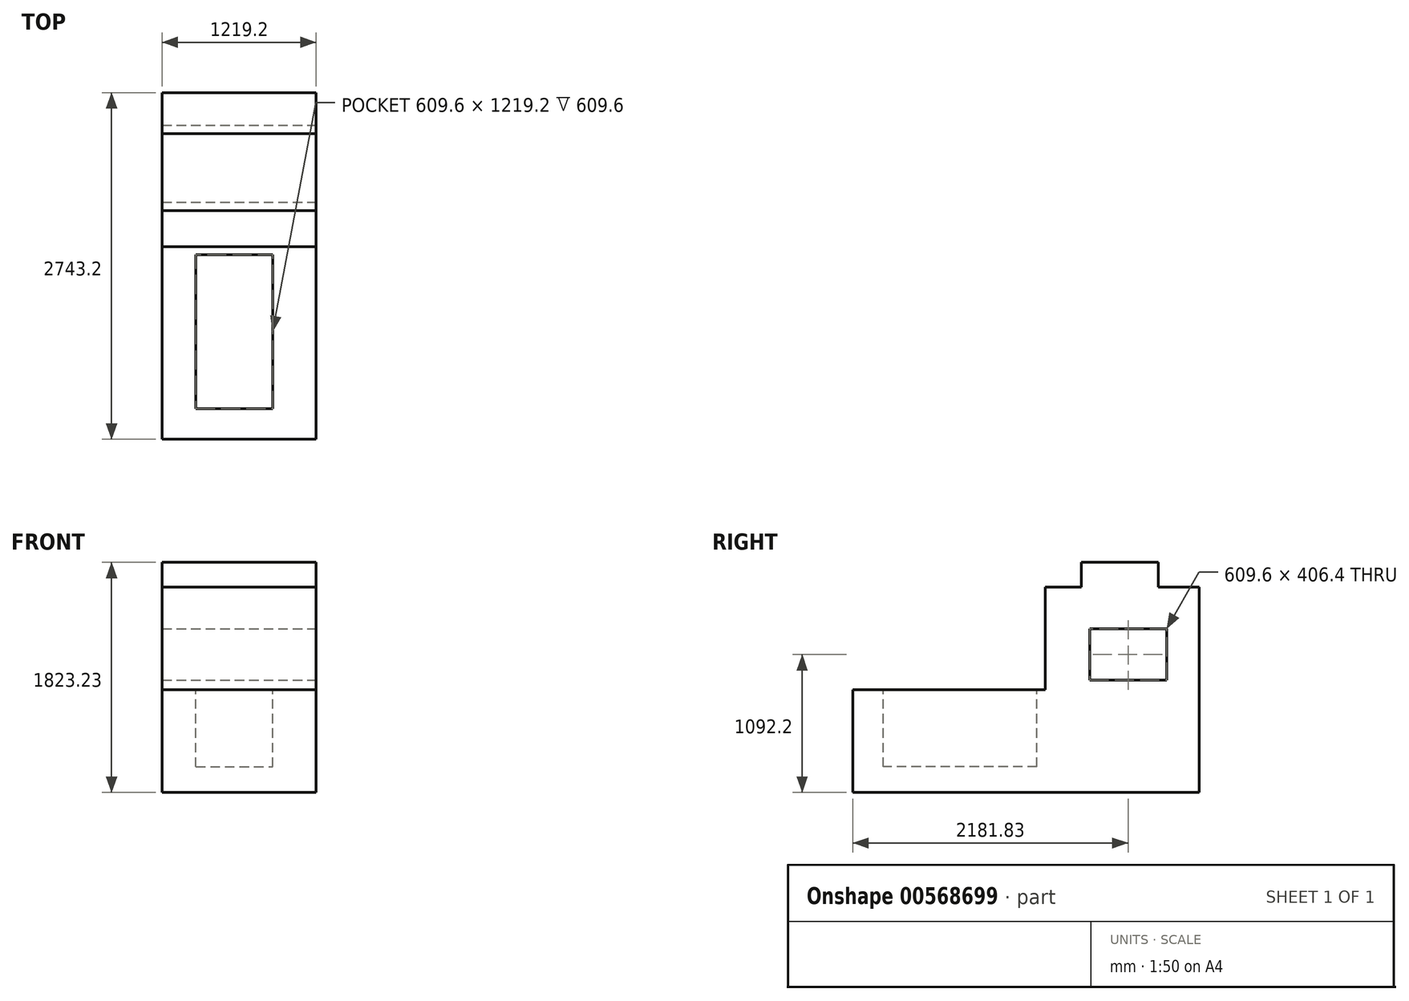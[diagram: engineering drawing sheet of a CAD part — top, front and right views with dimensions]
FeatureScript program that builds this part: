
annotation { "Feature Type Name" : "Feature", "Feature Type Description" : "" }
export const myFeature = defineFeature(function(context is Context, id is Id, definition is map)
    precondition{}
    {
        {
            var Q0;
            Q0=qCreatedBy(makeId("Front.planeOp"),FACE);
            var sketch = newSketch(context, id + "F0", { "sketchPlane" : qUnion([Q0])});
            skLineSegment(sketch, "E0.bottom", {"start": v(0, 0) * mm, "end": v(1219.2, 0) * mm});
            skLineSegment(sketch, "E0.top", {"start": v(0, 812.8) * mm, "end": v(1219.2, 812.8) * mm});
            skLineSegment(sketch, "E0.left", {"start": v(0, 0) * mm, "end": v(0, 812.8) * mm});
            skLineSegment(sketch, "E0.right", {"start": v(1219.2, 0) * mm, "end": v(1219.2, 812.8) * mm});
            skSolve(sketch);
        }
        {
            var Q0;
            Q0 = qSketchRegion(id + "F0", true);
            extrude(context, id + "F1", {"entities" : qUnion([Q0]), "depth" : 2743.2 * mm, "offsetDistance" : 25.4 * mm});
        }
        {
            var Q0;
            Q0=makeQuery(id+"F1.opExtrude","SWEPT_FACE",FACE,{"disambiguationData":[OSD([sQuery(id+"F0.wireOp",EDGE,"E0.right")])]});
            var sketch = newSketch(context, id + "F2", { "sketchPlane" : qUnion([Q0])});
            skLineSegment(sketch, "E1.bottom", {"start": v(0, 812.8) * mm, "end": v(-1219.2, 812.8) * mm});
            skLineSegment(sketch, "E1.top", {"start": v(0, 1625.6) * mm, "end": v(-1219.2, 1625.6) * mm});
            skLineSegment(sketch, "E1.left", {"start": v(0, 812.8) * mm, "end": v(0, 1625.6) * mm});
            skLineSegment(sketch, "E1.right", {"start": v(-1219.2, 812.8) * mm, "end": v(-1219.2, 1625.6) * mm});
            skSolve(sketch);
        }
        {
            var Q0;
            Q0=makeQuery(id+"F2.imprint","IMPRINT",FACE,{"disambiguationData":[TD([[makeQuery(id+"F2.imprint","IMPRINT",EDGE,{"derivedFrom":sQuery(id+"F2.wireOp",EDGE,"E1.bottom")}),1.0]])]});
            extrude(context, id + "F3", {"entities" : qUnion([Q0]), "operationType" : NewBodyOperationType.ADD, "oppositeDirection" : true, "depth" : 1219.2 * mm, "offsetDistance" : 25.4 * mm});
        }
        {
            var Q0;
            Q0=makeQuery(id+"F3.boolean.opBoolean","MERGE",FACE,{"derivedFrom":[makeQuery(id+"F1.opExtrude","SWEPT_FACE",FACE,{"disambiguationData":[OSD([sQuery(id+"F0.wireOp",EDGE,"E0.right")])]}),makeQuery(id+"F3.opExtrude","CAP_FACE",FACE,{"disambiguationData":[OSD([sQuery(id+"F2.wireOp",EDGE,"E1.bottom"),sQuery(id+"F2.wireOp",EDGE,"E1.top"),sQuery(id+"F2.wireOp",EDGE,"E1.left"),sQuery(id+"F2.wireOp",EDGE,"E1.right")])],"isStart":true})]});
            var sketch = newSketch(context, id + "F4", { "sketchPlane" : qUnion([Q0])});
            skSolve(sketch);
        }
        {
            var Q0;
            {var subQ0=sQuery(id+"F0.wireOp",EDGE,"E0.right");Q0=makeQuery(id+"F4.imprint","IMPRINT",FACE,{"disambiguationData":[TD([[makeQuery(id+"F4.imprint","IMPRINT",EDGE,{"derivedFrom":makeQuery(id+"F1.opExtrude","CAP_EDGE",EDGE,{"disambiguationData":[OSD([subQ0])],"isStart":false})}),-1.0]])]});}
            var sketch = newSketch(context, id + "F5", { "sketchPlane" : qUnion([Q0])});
            skLineSegment(sketch, "E2.bottom", {"start": v(-932.01, 1620.03) * mm, "end": v(-322.41, 1620.03) * mm});
            skLineSegment(sketch, "E2.top", {"start": v(-932.01, 1823.23) * mm, "end": v(-322.41, 1823.23) * mm});
            skLineSegment(sketch, "E2.left", {"start": v(-932.01, 1620.03) * mm, "end": v(-932.01, 1823.23) * mm});
            skLineSegment(sketch, "E2.right", {"start": v(-322.41, 1620.03) * mm, "end": v(-322.41, 1823.23) * mm});
            skSolve(sketch);
        }
        {
            var Q0;
            {var subQ0=sQuery(id+"F5.wireOp",EDGE,"E2.top");Q0=makeQuery(id+"F5.imprint","IMPRINT",FACE,{"disambiguationData":[TD([[makeQuery(id+"F5.imprint","IMPRINT",EDGE,{"derivedFrom":subQ0}),-1.0]])]});}
            extrude(context, id + "F6", {"entities" : qUnion([Q0]), "operationType" : NewBodyOperationType.ADD, "oppositeDirection" : true, "depth" : 1219.2 * mm, "offsetDistance" : 25.4 * mm});
        }
        {
            var Q0;
            {var subQ0=sQuery(id+"F0.wireOp",EDGE,"E0.right");Q0=makeQuery(id+"F4.imprint","IMPRINT",FACE,{"disambiguationData":[TD([[makeQuery(id+"F4.imprint","IMPRINT",EDGE,{"derivedFrom":makeQuery(id+"F1.opExtrude","CAP_EDGE",EDGE,{"disambiguationData":[OSD([subQ0])],"isStart":false})}),-1.0]])]});}
            var sketch = newSketch(context, id + "F7", { "sketchPlane" : qUnion([Q0])});
            skLineSegment(sketch, "E3.bottom", {"start": v(-866.17, 1295.4) * mm, "end": v(-256.57, 1295.4) * mm});
            skLineSegment(sketch, "E3.top", {"start": v(-866.17, 889) * mm, "end": v(-256.57, 889) * mm});
            skLineSegment(sketch, "E3.left", {"start": v(-866.17, 1295.4) * mm, "end": v(-866.17, 889) * mm});
            skLineSegment(sketch, "E3.right", {"start": v(-256.57, 1295.4) * mm, "end": v(-256.57, 889) * mm});
            skSolve(sketch);
        }
        {
            var Q0;
            Q0 = qSketchRegion(id + "F7", true);
            extrude(context, id + "F8", {"entities" : qUnion([Q0]), "operationType" : NewBodyOperationType.REMOVE, "oppositeDirection" : true, "depth" : 1219.2 * mm, "offsetDistance" : 25.4 * mm});
        }
        {
            var Q0;
            Q0=makeQuery(id+"F1.opExtrude","SWEPT_FACE",FACE,{"disambiguationData":[OSD([sQuery(id+"F0.wireOp",EDGE,"E0.top")])]});
            var sketch = newSketch(context, id + "F9", { "sketchPlane" : qUnion([Q0])});
            skLineSegment(sketch, "E4.bottom", {"start": v(267.95, -1282.87) * mm, "end": v(877.55, -1282.87) * mm});
            skLineSegment(sketch, "E4.top", {"start": v(267.95, -2502.07) * mm, "end": v(877.55, -2502.07) * mm});
            skLineSegment(sketch, "E4.left", {"start": v(267.95, -1282.87) * mm, "end": v(267.95, -2502.07) * mm});
            skLineSegment(sketch, "E4.right", {"start": v(877.55, -1282.87) * mm, "end": v(877.55, -2502.07) * mm});
            skSolve(sketch);
        }
        {
            var Q0;
            Q0 = qSketchRegion(id + "F9", true);
            extrude(context, id + "F10", {"entities" : qUnion([Q0]), "operationType" : NewBodyOperationType.REMOVE, "oppositeDirection" : true, "depth" : 609.6 * mm, "offsetDistance" : 25.4 * mm});
        }
    });
